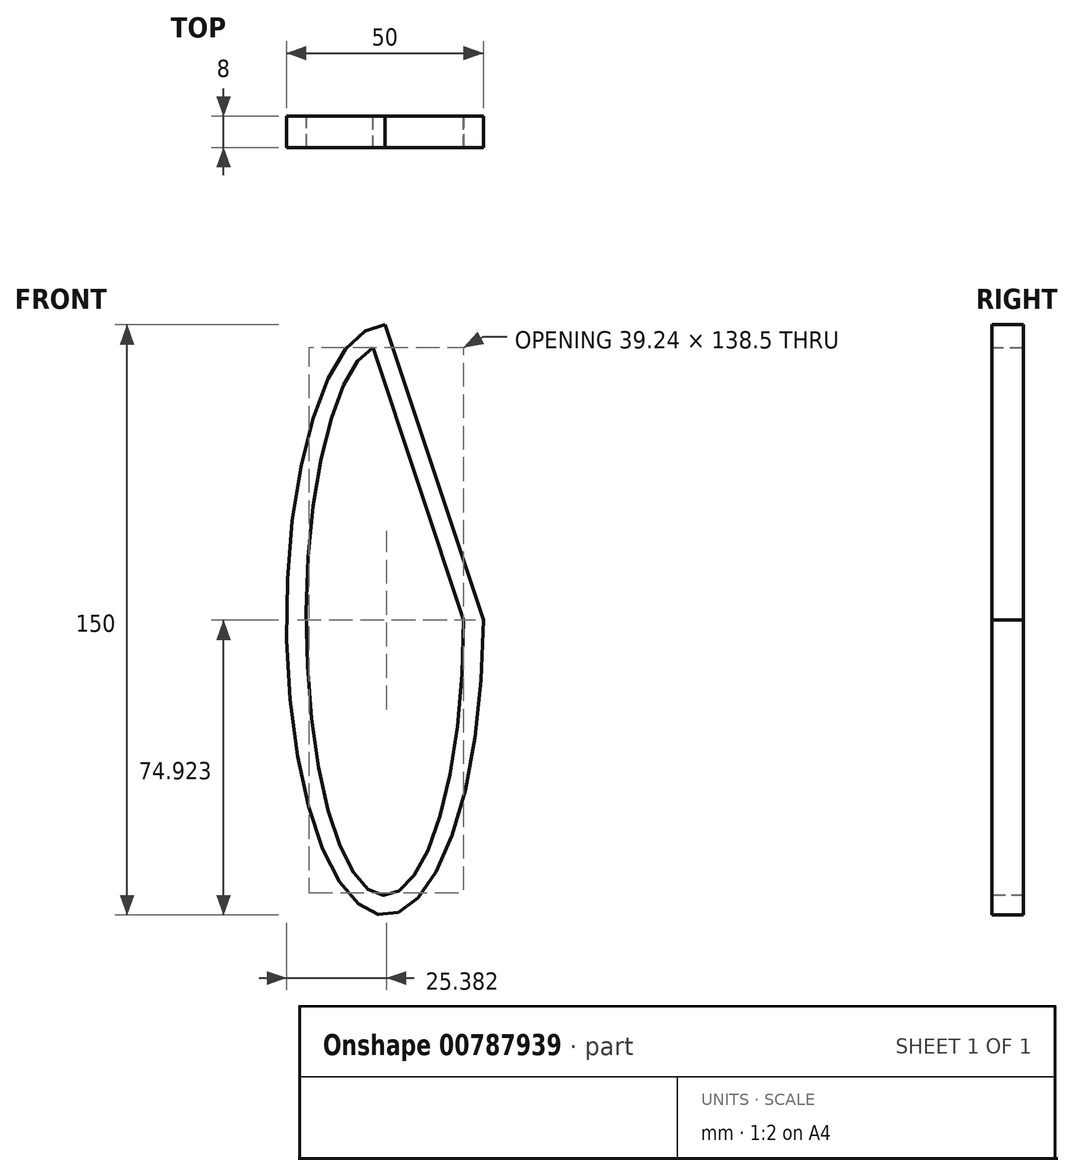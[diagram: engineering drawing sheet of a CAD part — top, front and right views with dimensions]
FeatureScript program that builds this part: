
annotation { "Feature Type Name" : "Feature", "Feature Type Description" : "" }
export const myFeature = defineFeature(function(context is Context, id is Id, definition is map)
    precondition{}
    {
        {
            var Q0;
            Q0=qCreatedBy(makeId("Front.planeOp"),FACE);
            var sketch = newSketch(context, id + "F0", { "sketchPlane" : qUnion([Q0])});
            skEllipse(sketch, "E0", {"center": v(0, 0) * mm, "majorRadius": 75 * mm, "minorRadius": 25 * mm, "majorAxis": v(0, -1)});
            skSolve(sketch);
        }
        {
            var Q0;
            Q0 = qSketchRegion(id + "F0", true);
            extrude(context, id + "F1", {"entities" : qUnion([Q0]), "depth" : 8 * mm, "offsetDistance" : 25 * mm});
        }
        {
            var Q0;
            Q0=makeQuery(id+"F1.opExtrude","CAP_FACE",FACE,{"disambiguationData":[OSD([sQuery(id+"F0.wireOp",EDGE,"E0")])],"isStart":false});
            var sketch = newSketch(context, id + "F2", { "sketchPlane" : qUnion([Q0])});
            skLineSegment(sketch, "E1", {"start": v(0, 75) * mm, "end": v(25, 0) * mm});
            skLineSegment(sketch, "E2", {"start": v(25, 0) * mm, "end": v(25, 74.97) * mm});
            skLineSegment(sketch, "E3", {"start": v(25, 74.97) * mm, "end": v(0, 75) * mm});
            skSolve(sketch);
        }
        {
            var Q0;
            Q0 = qSketchRegion(id + "F2", true);
            extrude(context, id + "F3", {"entities" : qUnion([Q0]), "operationType" : NewBodyOperationType.REMOVE, "endBound" : BoundingType.THROUGH_ALL, "oppositeDirection" : true, "depth" : 25 * mm, "offsetDistance" : 25 * mm});
        }
        {
            var Q0;
            Q0=qCreatedBy(makeId("Front.planeOp"),FACE);
            var sketch = newSketch(context, id + "F4", { "sketchPlane" : qUnion([Q0])});
            skEllipse(sketch, "E4", {"center": v(0, 0) * mm, "majorRadius": 70 * mm, "minorRadius": 20 * mm, "majorAxis": v(0, -1)});
            skSolve(sketch);
        }
        {
            var Q0;
            Q0 = qSketchRegion(id + "F4", true);
            extrude(context, id + "F5", {"entities" : qUnion([Q0]), "operationType" : NewBodyOperationType.REMOVE, "endBound" : BoundingType.THROUGH_ALL, "depth" : 25 * mm, "offsetDistance" : 25 * mm});
        }
        {
            var Q0;
            Q0=qCreatedBy(makeId("Front.planeOp"),FACE);
            var sketch = newSketch(context, id + "F6", { "sketchPlane" : qUnion([Q0])});
            skLineSegment(sketch, "E5", {"start": v(25, 0) * mm, "end": v(0, 74.99) * mm});
            skLineSegment(sketch, "E6", {"start": v(25, 0) * mm, "end": v(20, 0) * mm});
            skLineSegment(sketch, "E7", {"start": v(20, 0) * mm, "end": v(-4.57, 73.69) * mm});
            skLineSegment(sketch, "E8", {"start": v(-4.57, 73.69) * mm, "end": v(0, 74.99) * mm});
            skSolve(sketch);
        }
        {
            var Q0;
            Q0=makeQuery(id+"F6.imprint","IMPRINT",FACE,{"disambiguationData":[TD([[makeQuery(id+"F6.imprint","IMPRINT",EDGE,{"derivedFrom":sQuery(id+"F6.wireOp",EDGE,"E5")}),1.0]])]});
            extrude(context, id + "F7", {"entities" : qUnion([Q0]), "operationType" : NewBodyOperationType.ADD, "depth" : 8 * mm, "offsetDistance" : 25 * mm});
        }
    });
